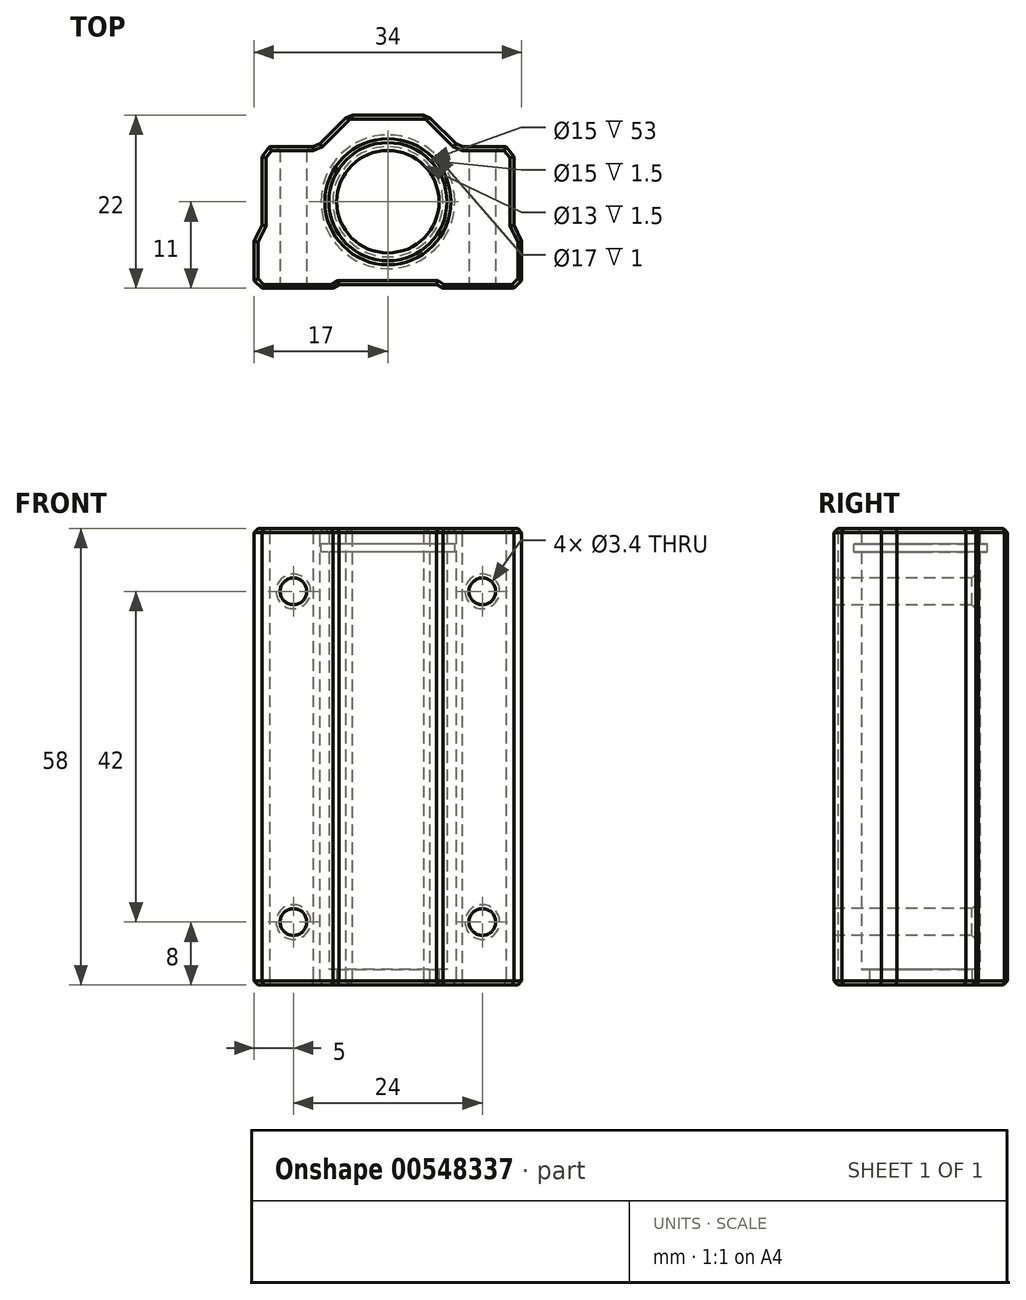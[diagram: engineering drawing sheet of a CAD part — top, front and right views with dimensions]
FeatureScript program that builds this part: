
annotation { "Feature Type Name" : "Feature", "Feature Type Description" : "" }
export const myFeature = defineFeature(function(context is Context, id is Id, definition is map)
    precondition{}
    {
        {
            var Q0;
            Q0=qCreatedBy(makeId("Top.planeOp"),FACE);
            var sketch = newSketch(context, id + "F0", { "sketchPlane" : qUnion([Q0])});
            skLineSegment(sketch, "E0", {"start": v(16, -11) * mm, "end": v(17, -10) * mm});
            skLineSegment(sketch, "E1", {"start": v(17, -10) * mm, "end": v(17, -5) * mm});
            skLineSegment(sketch, "E2", {"start": v(17, -5) * mm, "end": v(16, -3) * mm});
            skLineSegment(sketch, "E3", {"start": v(16, -3) * mm, "end": v(16, 5.75) * mm});
            skLineSegment(sketch, "E4", {"start": v(16, 5.75) * mm, "end": v(15, 7) * mm});
            skLineSegment(sketch, "E5", {"start": v(15, 7) * mm, "end": v(9, 7) * mm});
            skLineSegment(sketch, "E6", {"start": v(9, 7) * mm, "end": v(5, 11) * mm});
            skLineSegment(sketch, "E7", {"start": v(5, 11) * mm, "end": v(-5, 11) * mm});
            skLineSegment(sketch, "E8", {"start": v(-5, 11) * mm, "end": v(-9, 7) * mm});
            skLineSegment(sketch, "E9", {"start": v(-9, 7) * mm, "end": v(-15, 7) * mm});
            skLineSegment(sketch, "E10", {"start": v(-15, 7) * mm, "end": v(-16, 5.75) * mm});
            skLineSegment(sketch, "E11", {"start": v(-16, 5.75) * mm, "end": v(-16, -3) * mm});
            skLineSegment(sketch, "E12", {"start": v(-16, -3) * mm, "end": v(-17, -5) * mm});
            skLineSegment(sketch, "E13", {"start": v(-17, -5) * mm, "end": v(-17, -10) * mm});
            skLineSegment(sketch, "E14", {"start": v(-17, -10) * mm, "end": v(-16, -11) * mm});
            skCircle(sketch, "E15", {"center": v(0, 0) * mm, "radius": 7.5 * mm});
            skLineSegment(sketch, "E16", {"start": v(-16, -11) * mm, "end": v(-7, -11) * mm});
            skLineSegment(sketch, "E17", {"start": v(-7, -11) * mm, "end": v(-6.2, -10.5) * mm});
            skLineSegment(sketch, "E18", {"start": v(-6.2, -10.5) * mm, "end": v(6.2, -10.5) * mm});
            skLineSegment(sketch, "E19", {"start": v(6.2, -10.5) * mm, "end": v(7, -11) * mm});
            skLineSegment(sketch, "E20", {"start": v(7, -11) * mm, "end": v(16, -11) * mm});
            skSolve(sketch);
        }
        {
            var Q0;
            Q0=qSketchRegion(id+"F0",true);
            extrude(context, id + "F1", {"entities" : qUnion([Q0]), "depth" : 29 * mm, "offsetDistance" : 25 * mm, "hasSecondDirection" : true, "secondDirectionOppositeDirection" : true, "secondDirectionDepth" : 29 * mm});
        }
        {
            var Q0;
            Q0=makeQuery(id+"F1.opExtrude","SWEPT_FACE",FACE,{"disambiguationData":[OSD([sQuery(id+"F0.wireOp",EDGE,"E16")])]});
            var sketch = newSketch(context, id + "F2", { "sketchPlane" : qUnion([Q0])});
            skCircle(sketch, "E21", {"center": v(-12, 21) * mm, "radius": 1.7 * mm});
            skCircle(sketch, "E22", {"center": v(-12, -21) * mm, "radius": 1.7 * mm});
            skCircle(sketch, "E23", {"center": v(12, 21) * mm, "radius": 1.7 * mm});
            skCircle(sketch, "E24", {"center": v(12, -21) * mm, "radius": 1.7 * mm});
            skSolve(sketch);
        }
        {
            var Q0;
            Q0=makeQuery(id+"F2.imprint","IMPRINT",FACE,{"disambiguationData":[TD([[makeQuery(id+"F2.imprint","IMPRINT",EDGE,{"derivedFrom":sQuery(id+"F2.wireOp",EDGE,"E21")}),1.0]])]});
            var Q1;
            Q1=makeQuery(id+"F2.imprint","IMPRINT",FACE,{"disambiguationData":[TD([[makeQuery(id+"F2.imprint","IMPRINT",EDGE,{"derivedFrom":sQuery(id+"F2.wireOp",EDGE,"E23")}),1.0]])]});
            var Q2;
            Q2=makeQuery(id+"F2.imprint","IMPRINT",FACE,{"disambiguationData":[TD([[makeQuery(id+"F2.imprint","IMPRINT",EDGE,{"derivedFrom":sQuery(id+"F2.wireOp",EDGE,"E24")}),1.0]])]});
            var Q3;
            Q3=makeQuery(id+"F2.imprint","IMPRINT",FACE,{"disambiguationData":[TD([[makeQuery(id+"F2.imprint","IMPRINT",EDGE,{"derivedFrom":sQuery(id+"F2.wireOp",EDGE,"E22")}),1.0]])]});
            var Q4;
            Q4=sQuery(id+"F2.wireOp",EDGE,"E22");
            var Q5;
            Q5=sQuery(id+"F2.wireOp",EDGE,"E21");
            var Q6;
            Q6=sQuery(id+"F2.wireOp",EDGE,"E23");
            var Q7;
            Q7=sQuery(id+"F2.wireOp",EDGE,"E24");
            extrude(context, id + "F3", {"entities" : qUnion([Q0, Q1, Q2, Q3]), "operationType" : NewBodyOperationType.REMOVE, "surfaceEntities" : qUnion([Q4, Q5, Q6, Q7]), "oppositeDirection" : true, "depth" : 25 * mm, "offsetDistance" : 25 * mm});
        }
        {
            var Q0;
            Q0=makeQuery(id+"F3.boolean.opBoolean","INTERSECT",EDGE,{"derivedFrom":[makeQuery(id+"F1.opExtrude","SWEPT_FACE",FACE,{"disambiguationData":[OSD([sQuery(id+"F0.wireOp",EDGE,"E9")])]}),makeQuery(id+"F3.opExtrude","SWEPT_FACE",FACE,{"disambiguationData":[OSD([sQuery(id+"F2.wireOp",EDGE,"E21")])]})]});
            var Q1;
            Q1=makeQuery(id+"F3.boolean.opBoolean","INTERSECT",EDGE,{"derivedFrom":[makeQuery(id+"F1.opExtrude","SWEPT_FACE",FACE,{"disambiguationData":[OSD([sQuery(id+"F0.wireOp",EDGE,"E9")])]}),makeQuery(id+"F3.opExtrude","SWEPT_FACE",FACE,{"disambiguationData":[OSD([sQuery(id+"F2.wireOp",EDGE,"E22")])]})]});
            var Q2;
            Q2=makeQuery(id+"F3.boolean.opBoolean","INTERSECT",EDGE,{"derivedFrom":[makeQuery(id+"F1.opExtrude","SWEPT_FACE",FACE,{"disambiguationData":[OSD([sQuery(id+"F0.wireOp",EDGE,"E5")])]}),makeQuery(id+"F3.opExtrude","SWEPT_FACE",FACE,{"disambiguationData":[OSD([sQuery(id+"F2.wireOp",EDGE,"E24")])]})]});
            var Q3;
            Q3=makeQuery(id+"F3.boolean.opBoolean","INTERSECT",EDGE,{"derivedFrom":[makeQuery(id+"F1.opExtrude","SWEPT_FACE",FACE,{"disambiguationData":[OSD([sQuery(id+"F0.wireOp",EDGE,"E5")])]}),makeQuery(id+"F3.opExtrude","SWEPT_FACE",FACE,{"disambiguationData":[OSD([sQuery(id+"F2.wireOp",EDGE,"E23")])]})]});
            var Q4;
            Q4=makeQuery(id+"F3.boolean.opBoolean","COPY",EDGE,{"derivedFrom":makeQuery(id+"F3.opExtrude","CAP_EDGE",EDGE,{"disambiguationData":[OSD([sQuery(id+"F2.wireOp",EDGE,"E21")])],"isStart":true})});
            var Q5;
            Q5=makeQuery(id+"F3.boolean.opBoolean","COPY",EDGE,{"derivedFrom":makeQuery(id+"F3.opExtrude","CAP_EDGE",EDGE,{"disambiguationData":[OSD([sQuery(id+"F2.wireOp",EDGE,"E22")])],"isStart":true})});
            var Q6;
            Q6=makeQuery(id+"F3.boolean.opBoolean","COPY",EDGE,{"derivedFrom":makeQuery(id+"F3.opExtrude","CAP_EDGE",EDGE,{"disambiguationData":[OSD([sQuery(id+"F2.wireOp",EDGE,"E24")])],"isStart":true})});
            var Q7;
            Q7=makeQuery(id+"F3.boolean.opBoolean","COPY",EDGE,{"derivedFrom":makeQuery(id+"F3.opExtrude","CAP_EDGE",EDGE,{"disambiguationData":[OSD([sQuery(id+"F2.wireOp",EDGE,"E23")])],"isStart":true})});
            chamfer(context, id + "F4", {"entities" : qUnion([Q0, Q1, Q2, Q3, Q4, Q5, Q6, Q7]), "width" : .5 * mm, "tangentPropagation" : true});
        }
        {
            var Q0;
            Q0=makeQuery(id+"F1.opExtrude","CAP_FACE",FACE,{"disambiguationData":[OSD([sQuery(id+"F0.wireOp",EDGE,"E0"),sQuery(id+"F0.wireOp",EDGE,"E1"),sQuery(id+"F0.wireOp",EDGE,"E2"),sQuery(id+"F0.wireOp",EDGE,"E3"),sQuery(id+"F0.wireOp",EDGE,"E4"),sQuery(id+"F0.wireOp",EDGE,"E5"),sQuery(id+"F0.wireOp",EDGE,"E6"),sQuery(id+"F0.wireOp",EDGE,"E7"),sQuery(id+"F0.wireOp",EDGE,"E8"),sQuery(id+"F0.wireOp",EDGE,"E9"),sQuery(id+"F0.wireOp",EDGE,"E10"),sQuery(id+"F0.wireOp",EDGE,"E11"),sQuery(id+"F0.wireOp",EDGE,"E12"),sQuery(id+"F0.wireOp",EDGE,"E13"),sQuery(id+"F0.wireOp",EDGE,"E14"),sQuery(id+"F0.wireOp",EDGE,"E15"),sQuery(id+"F0.wireOp",EDGE,"E16"),sQuery(id+"F0.wireOp",EDGE,"E17"),sQuery(id+"F0.wireOp",EDGE,"E18"),sQuery(id+"F0.wireOp",EDGE,"E19"),sQuery(id+"F0.wireOp",EDGE,"E20")])],"isStart":true});
            var sketch = newSketch(context, id + "F5", { "sketchPlane" : qUnion([Q0])});
            skCircle(sketch, "E25", {"center": v(0, 0) * mm, "radius": 6.5 * mm});
            skSolve(sketch);
        }
        {
            var Q0;
            Q0=makeQuery(id+"F5.imprint","IMPRINT",FACE,{"disambiguationData":[TD([[makeQuery(id+"F5.imprint","IMPRINT",EDGE,{"derivedFrom":sQuery(id+"F5.wireOp",EDGE,"E25")}),-1.0]])]});
            extrude(context, id + "F6", {"entities" : qUnion([Q0]), "operationType" : NewBodyOperationType.ADD, "oppositeDirection" : true, "depth" : 2 * mm, "offsetDistance" : 25 * mm});
        }
        {
            var Q0;
            Q0=makeQuery(id+"F1.opExtrude","CAP_FACE",FACE,{"disambiguationData":[OSD([sQuery(id+"F0.wireOp",EDGE,"E0"),sQuery(id+"F0.wireOp",EDGE,"E1"),sQuery(id+"F0.wireOp",EDGE,"E2"),sQuery(id+"F0.wireOp",EDGE,"E3"),sQuery(id+"F0.wireOp",EDGE,"E4"),sQuery(id+"F0.wireOp",EDGE,"E5"),sQuery(id+"F0.wireOp",EDGE,"E6"),sQuery(id+"F0.wireOp",EDGE,"E7"),sQuery(id+"F0.wireOp",EDGE,"E8"),sQuery(id+"F0.wireOp",EDGE,"E9"),sQuery(id+"F0.wireOp",EDGE,"E10"),sQuery(id+"F0.wireOp",EDGE,"E11"),sQuery(id+"F0.wireOp",EDGE,"E12"),sQuery(id+"F0.wireOp",EDGE,"E13"),sQuery(id+"F0.wireOp",EDGE,"E14"),sQuery(id+"F0.wireOp",EDGE,"E15"),sQuery(id+"F0.wireOp",EDGE,"E16"),sQuery(id+"F0.wireOp",EDGE,"E17"),sQuery(id+"F0.wireOp",EDGE,"E18"),sQuery(id+"F0.wireOp",EDGE,"E19"),sQuery(id+"F0.wireOp",EDGE,"E20")])],"isStart":false});
            cPlane(context, id + "F7", {"entities" : qUnion([Q0]), "cplaneType" : CPlaneType.OFFSET, "offset" : 2 * mm, "oppositeDirection" : true, "width" : 150 * mm, "height" : 150 * mm});
        }
        {
            var Q0;
            Q0=qCreatedBy(id+"F7.planeOp",FACE);
            var sketch = newSketch(context, id + "F8", { "sketchPlane" : qUnion([Q0])});
            skCircle(sketch, "E26", {"center": v(0, 0) * mm, "radius": 8.5 * mm});
            skSolve(sketch);
        }
        {
            var Q0;
            Q0=qSketchRegion(id+"F8",true);
            extrude(context, id + "F9", {"entities" : qUnion([Q0]), "operationType" : NewBodyOperationType.REMOVE, "oppositeDirection" : true, "depth" : 1 * mm, "offsetDistance" : 25 * mm});
        }
        {
            var Q0;
            Q0=makeQuery(id+"F1.opExtrude","CAP_FACE",FACE,{"disambiguationData":[OSD([sQuery(id+"F0.wireOp",EDGE,"E0"),sQuery(id+"F0.wireOp",EDGE,"E1"),sQuery(id+"F0.wireOp",EDGE,"E2"),sQuery(id+"F0.wireOp",EDGE,"E3"),sQuery(id+"F0.wireOp",EDGE,"E4"),sQuery(id+"F0.wireOp",EDGE,"E5"),sQuery(id+"F0.wireOp",EDGE,"E6"),sQuery(id+"F0.wireOp",EDGE,"E7"),sQuery(id+"F0.wireOp",EDGE,"E8"),sQuery(id+"F0.wireOp",EDGE,"E9"),sQuery(id+"F0.wireOp",EDGE,"E10"),sQuery(id+"F0.wireOp",EDGE,"E11"),sQuery(id+"F0.wireOp",EDGE,"E12"),sQuery(id+"F0.wireOp",EDGE,"E13"),sQuery(id+"F0.wireOp",EDGE,"E14"),sQuery(id+"F0.wireOp",EDGE,"E15"),sQuery(id+"F0.wireOp",EDGE,"E16"),sQuery(id+"F0.wireOp",EDGE,"E17"),sQuery(id+"F0.wireOp",EDGE,"E18"),sQuery(id+"F0.wireOp",EDGE,"E19"),sQuery(id+"F0.wireOp",EDGE,"E20")])],"isStart":false});
            var Q1;
            {var subQ0=sQuery(id+"F0.wireOp",EDGE,"E15");Q1=makeQuery(id+"F6.boolean.opBoolean","MERGE",FACE,{"derivedFrom":[makeQuery(id+"F1.opExtrude","CAP_FACE",FACE,{"disambiguationData":[OSD([sQuery(id+"F0.wireOp",EDGE,"E0"),sQuery(id+"F0.wireOp",EDGE,"E1"),sQuery(id+"F0.wireOp",EDGE,"E2"),sQuery(id+"F0.wireOp",EDGE,"E3"),sQuery(id+"F0.wireOp",EDGE,"E4"),sQuery(id+"F0.wireOp",EDGE,"E5"),sQuery(id+"F0.wireOp",EDGE,"E6"),sQuery(id+"F0.wireOp",EDGE,"E7"),sQuery(id+"F0.wireOp",EDGE,"E8"),sQuery(id+"F0.wireOp",EDGE,"E9"),sQuery(id+"F0.wireOp",EDGE,"E10"),sQuery(id+"F0.wireOp",EDGE,"E11"),sQuery(id+"F0.wireOp",EDGE,"E12"),sQuery(id+"F0.wireOp",EDGE,"E13"),sQuery(id+"F0.wireOp",EDGE,"E14"),subQ0,sQuery(id+"F0.wireOp",EDGE,"E16"),sQuery(id+"F0.wireOp",EDGE,"E17"),sQuery(id+"F0.wireOp",EDGE,"E18"),sQuery(id+"F0.wireOp",EDGE,"E19"),sQuery(id+"F0.wireOp",EDGE,"E20")])],"isStart":true}),makeQuery(id+"F6.opExtrude","CAP_FACE",FACE,{"disambiguationData":[OSD([subQ0,sQuery(id+"F5.wireOp",EDGE,"E25")])],"isStart":true})]});}
            var Q2;
            Q2=makeQuery(id+"F1.opExtrude","SWEPT_EDGE",EDGE,{"disambiguationData":[OSD([sQuery(id+"F0.wireOp",EDGE,"E8"),sQuery(id+"F0.wireOp",EDGE,"E9")])]});
            var Q3;
            Q3=makeQuery(id+"F1.opExtrude","SWEPT_EDGE",EDGE,{"disambiguationData":[OSD([sQuery(id+"F0.wireOp",EDGE,"E7"),sQuery(id+"F0.wireOp",EDGE,"E8")])]});
            var Q4;
            Q4=makeQuery(id+"F1.opExtrude","SWEPT_EDGE",EDGE,{"disambiguationData":[OSD([sQuery(id+"F0.wireOp",EDGE,"E6"),sQuery(id+"F0.wireOp",EDGE,"E7")])]});
            var Q5;
            Q5=makeQuery(id+"F1.opExtrude","SWEPT_EDGE",EDGE,{"disambiguationData":[OSD([sQuery(id+"F0.wireOp",EDGE,"E5"),sQuery(id+"F0.wireOp",EDGE,"E6")])]});
            chamfer(context, id + "F10", {"entities" : qUnion([Q0, Q1, Q2, Q3, Q4, Q5]), "width" : .5 * mm, "tangentPropagation" : true});
        }
    });
